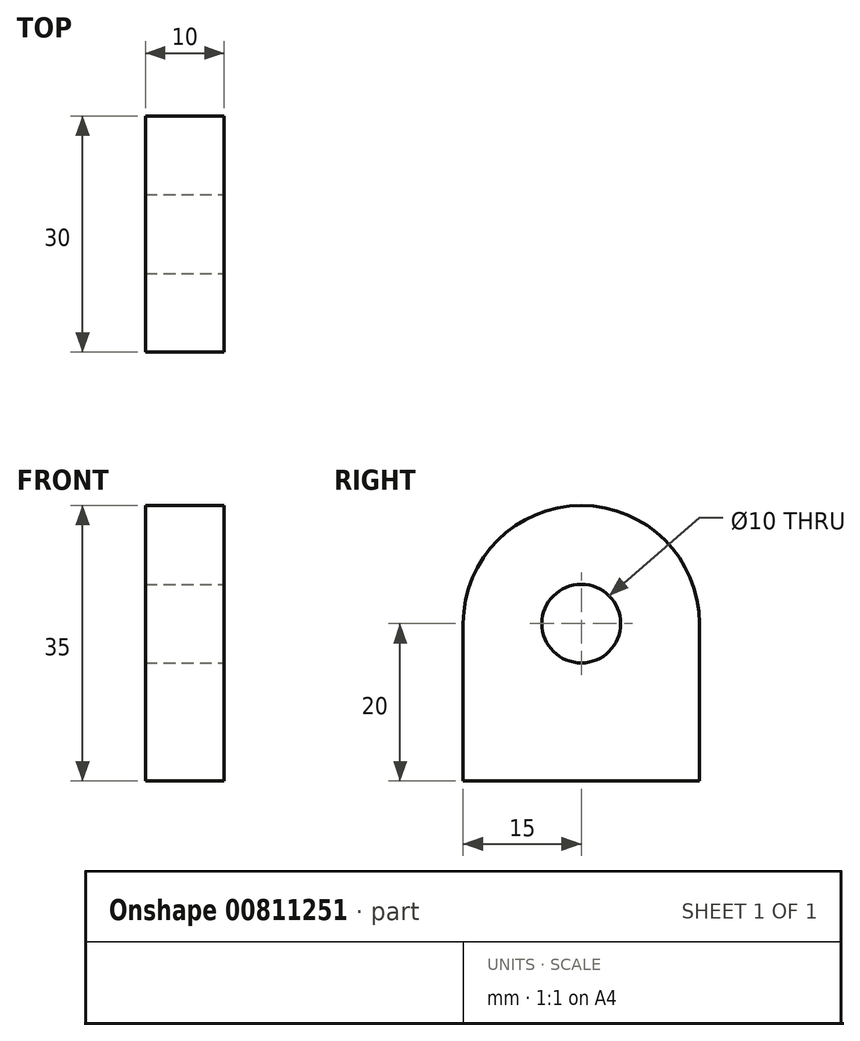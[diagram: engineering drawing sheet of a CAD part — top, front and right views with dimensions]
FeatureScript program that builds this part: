
annotation { "Feature Type Name" : "Feature", "Feature Type Description" : "" }
export const myFeature = defineFeature(function(context is Context, id is Id, definition is map)
    precondition{}
    {
        {
            var Q0;
            Q0=qCreatedBy(makeId("Top.planeOp"),FACE);
            var sketch = newSketch(context, id + "F0", { "sketchPlane" : qUnion([Q0])});
            skLineSegment(sketch, "E0", {"start": v(0, 0) * mm, "end": v(0, 8.44) * mm, "construction": true});
            skLineSegment(sketch, "E1", {"start": v(-20, 0) * mm, "end": v(20, 0) * mm, "construction": true});
            skArc(sketch, "E2.0.startCap", {"start": v(-20, -15) * mm, "mid": v(-35, 0) * mm, "end": v(-20, 15) * mm});
            skArc(sketch, "E2.0.endCap", {"start": v(20, 15) * mm, "mid": v(35, 0) * mm, "end": v(20, -15) * mm});
            skLineSegment(sketch, "E2.0.left", {"start": v(-20, 15) * mm, "end": v(20, 15) * mm});
            skLineSegment(sketch, "E2.0.right", {"start": v(-20, -15) * mm, "end": v(20, -15) * mm});
            skCircle(sketch, "E3", {"center": v(-20, 0) * mm, "radius": 5 * mm});
            skCircle(sketch, "E4", {"center": v(20, 0) * mm, "radius": 5 * mm});
            skLineSegment(sketch, "E5.bottom", {"start": v(5, 15) * mm, "end": v(-5, 15) * mm});
            skLineSegment(sketch, "E5.top", {"start": v(5, -15) * mm, "end": v(-5, -15) * mm});
            skLineSegment(sketch, "E5.left", {"start": v(5, 15) * mm, "end": v(5, -15) * mm});
            skLineSegment(sketch, "E5.right", {"start": v(-5, 15) * mm, "end": v(-5, -15) * mm});
            skPoint(sketch, "E5.middle", {"position": v(0, 0) * mm});
            skSolve(sketch);
        }
        {
            var Q0;
            {var subQ0=sQuery(id+"F0.wireOp",EDGE,"E5.left");var subQ8=makeQuery(id+"F0.imprint","IMPRINT",EDGE,{"derivedFrom":subQ0});var subQ10=sQuery(id+"F0.wireOp",EDGE,"E2.0.endCap");var subQ11=sQuery(id+"F0.wireOp",EDGE,"E2.0.startCap");Q0=qUnion([makeQuery(id+"F0.imprint","IMPRINT",FACE,{"disambiguationData":[TD([[makeQuery(id+"F0.imprint","IMPRINT",EDGE,{"derivedFrom":subQ11}),-1.0]])]}),makeQuery(id+"F0.imprint","IMPRINT",FACE,{"disambiguationData":[TD([[makeQuery(id+"F0.imprint","IMPRINT",EDGE,{"derivedFrom":subQ10}),-1.0]])]}),makeQuery(id+"F0.imprint","IMPRINT",FACE,{"disambiguationData":[TD([[subQ8,-1.0]])]})]);}
            extrude(context, id + "F1", {"entities" : qUnion([Q0]), "depth" : 10 * mm, "offsetDistance" : 25 * mm});
        }
        {
            var Q0;
            {var subQ0=sQuery(id+"F0.wireOp",EDGE,"E5.left");Q0=makeQuery(id+"F0.imprint","IMPRINT",FACE,{"disambiguationData":[TD([[makeQuery(id+"F0.imprint","IMPRINT",EDGE,{"derivedFrom":subQ0}),-1.0]])]});}
            extrude(context, id + "F2", {"entities" : qUnion([Q0]), "operationType" : NewBodyOperationType.ADD, "depth" : 35 * mm, "offsetDistance" : 25 * mm});
        }
        {
            var Q0;
            Q0=makeQuery(id+"F2.opExtrude","CAP_EDGE",EDGE,{"disambiguationData":[OSD([sQuery(id+"F0.wireOp",EDGE,"E2.0.right")])],"isStart":false});
            var Q1;
            Q1=makeQuery(id+"F2.opExtrude","CAP_EDGE",EDGE,{"disambiguationData":[OSD([sQuery(id+"F0.wireOp",EDGE,"E2.0.left")])],"isStart":false});
            fillet(context, id + "F3", {"entities" : qUnion([Q0, Q1]), "radius" : 15 * mm, "tangentPropagation" : true, "allowEdgeOverflow" : false});
        }
        {
            var Q0;
            Q0=makeQuery(id+"F2.opExtrude","SWEPT_FACE",FACE,{"disambiguationData":[OSD([sQuery(id+"F0.wireOp",EDGE,"E5.left")])]});
            var sketch = newSketch(context, id + "F4", { "sketchPlane" : qUnion([Q0])});
            skPoint(sketch, "E6", {"position": v(0, 20) * mm});
            skSolve(sketch);
        }
        {
            var Q0;
            Q0=sQuery(id+"F4.wireOp",VERTEX,"E6");
            var Q1;
            Q1=makeQuery(id+"F1.opExtrude","SWEPT_BODY",BODY,{"disambiguationData":[OSD([sQuery(id+"F0.wireOp",EDGE,"E2.0.startCap"),sQuery(id+"F0.wireOp",EDGE,"E2.0.endCap"),sQuery(id+"F0.wireOp",EDGE,"E2.0.left"),sQuery(id+"F0.wireOp",EDGE,"E2.0.right"),sQuery(id+"F0.wireOp",EDGE,"E3"),sQuery(id+"F0.wireOp",EDGE,"E4")])]});
            hole(context, id + "F5", {"style" : HoleStyle.SIMPLE, "endStyle" : HoleEndStyle.THROUGH, "holeDiameter" : 10 * mm, "majorDiameter" : 5 * mm, "tappedDepth" : 12 * mm, "tapClearance" : 3, "startFromSketch" : true, "locations" : qUnion([Q0]), "scope" : qUnion([Q1])});
        }
    });
